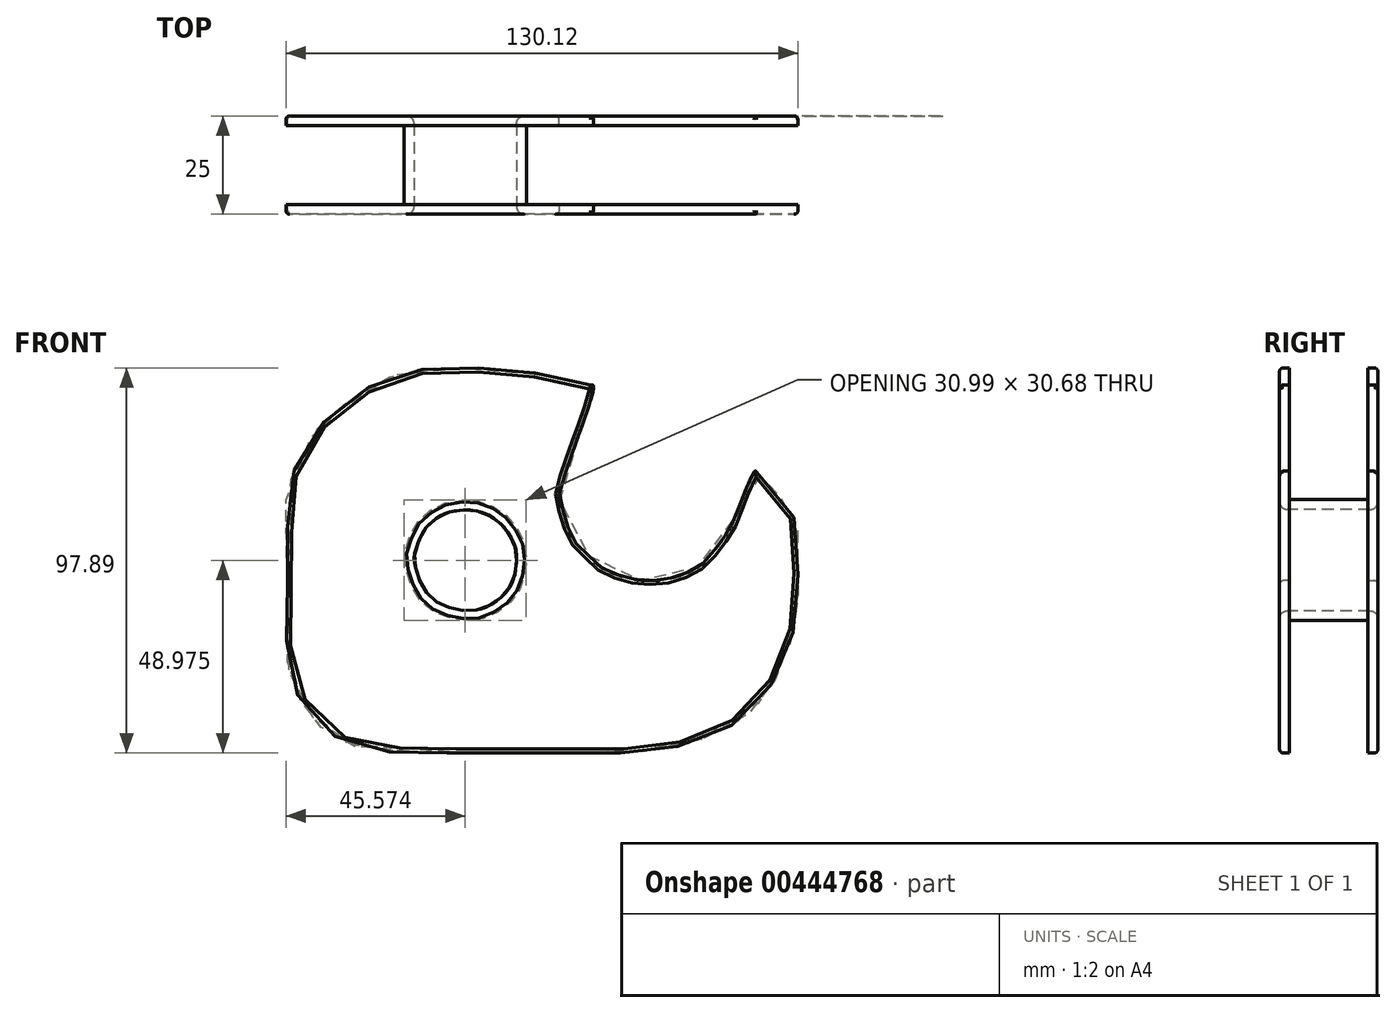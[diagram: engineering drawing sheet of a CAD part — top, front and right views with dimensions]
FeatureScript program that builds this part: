
annotation { "Feature Type Name" : "Feature", "Feature Type Description" : "" }
export const myFeature = defineFeature(function(context is Context, id is Id, definition is map)
    precondition{}
    {
        {
            var Q0;
            Q0=qCreatedBy(makeId("Front.planeOp"),FACE);
            var sketch = newSketch(context, id + "F0", { "sketchPlane" : qUnion([Q0])});
            skFitSpline(sketch, "E0", {"points": [v(-71.65, 26.42) * mm, v(-80.15, 0) * mm, v(-79.73, -4.2) * mm, v(-76.75, -12.5) * mm, v(-73.35, -16.11) * mm, v(-70.34, -19.08) * mm, v(-65.01, -21.68) * mm, v(-59.83, -22.83) * mm, v(-54.07, -22.76) * mm, v(-49.03, -21.39) * mm, v(-44.13, -18.8) * mm, v(-40.46, -14.7) * mm, v(-37.3, -10.23) * mm, v(-33.91, -2.3) * mm, v(-30.52, 4.9) * mm, v(-30.23, 4.68) * mm, v(-29.6, 4.1) * mm, v(-28.61, 3.17) * mm, v(-25.13, -0.54) * mm, v(-21.54, -5.47) * mm, v(-20.03, -8.48) * mm, v(-19.8, -11.5) * mm, v(-19.69, -25.69) * mm, v(-19.98, -30.15) * mm, v(-20.5, -33.92) * mm, v(-21.2, -37.17) * mm, v(-24.25, -46.03) * mm, v(-27.58, -50.92) * mm, v(-30.7, -55.25) * mm, v(-35.14, -58.91) * mm, v(-42.69, -62.76) * mm, v(-51.54, -65.35) * mm, v(-59.4, -66.43) * mm, v(-67.19, -66.7) * mm, v(-123.65, -66.4) * mm, v(-130.85, -65.55) * mm, v(-134.45, -64.1) * mm, v(-138.48, -61.87) * mm, v(-141.22, -59.78) * mm, v(-143.02, -57.55) * mm, v(-144.53, -55.54) * mm, v(-147.41, -50.86) * mm, v(-148.85, -46.68) * mm, v(-149.43, -43.08) * mm, v(-149.64, -40.27) * mm, v(-149.44, -8.11) * mm, v(-149.44, 0) * mm, v(-143.27, 13.63) * mm, v(-139.85, 17.57) * mm, v(-134.7, 22.02) * mm, v(-127.52, 26.82) * mm, v(-121.35, 29.56) * mm, v(-114.84, 30.76) * mm, v(-110.6, 31.06) * mm, v(-97.42, 30.92) * mm, v(-86.18, 29.77) * mm, v(-80.71, 28.62) * mm, v(-77.4, 27.9) * mm, v(-72.93, 26.74) * mm, v(-71.65, 26.42) * mm]});
            skSolve(sketch);
        }
        {
            var Q0;
            Q0=makeQuery(id+"F0.imprint","IMPRINT",FACE,{"disambiguationData":[TD([[makeQuery(id+"F0.imprint","IMPRINT",EDGE,{"derivedFrom":sQuery(id+"F0.wireOp",EDGE,"E0")}),-1.0]])]});
            var sketch = newSketch(context, id + "F1", { "sketchPlane" : qUnion([Q0])});
            skFitSpline(sketch, "E1", {"points": [v(-104.6, -4.98) * mm, v(-104.12, -4.9) * mm, v(-102.76, -5.01) * mm, v(-101.52, -5.2) * mm, v(-100.25, -5.56) * mm, v(-99.03, -5.95) * mm, v(-96.86, -7.2) * mm, v(-94.55, -9.13) * mm, v(-92.59, -12) * mm, v(-91.25, -15.64) * mm, v(-91.34, -19.3) * mm, v(-91.7, -21.7) * mm, v(-92.68, -24.2) * mm, v(-94.73, -26.9) * mm, v(-99.43, -29.92) * mm, v(-103.55, -30.64) * mm, v(-107.66, -30) * mm, v(-112.4, -27.77) * mm, v(-115, -24.56) * mm, v(-116.06, -22.14) * mm, v(-117.14, -18.03) * mm, v(-117.14, -16.42) * mm, v(-116.78, -15.26) * mm, v(-116.42, -14) * mm, v(-115.63, -11.94) * mm, v(-114.55, -9.93) * mm, v(-112.13, -7.6) * mm, v(-109.14, -5.78) * mm, v(-106.1, -5.17) * mm, v(-104.6, -4.98) * mm]});
            skSolve(sketch);
        }
        {
            var Q0;
            Q0=makeQuery(id+"F1.imprint","IMPRINT",FACE,{"disambiguationData":[TD([[makeQuery(id+"F1.imprint","IMPRINT",EDGE,{"derivedFrom":sQuery(id+"F1.wireOp",EDGE,"E1")}),1.0]])]});
            extrude(context, id + "F2", {"entities" : qUnion([Q0]), "depth" : 25 * mm});
        }
        {
            var Q0;
            Q0=makeQuery(id+"F2.opExtrude","SWEPT_FACE",FACE,{"disambiguationData":[OSD([sQuery(id+"F0.wireOp",EDGE,"E0")])]});
            shell(context, id + "F3", {"entities" : qUnion([Q0]), "thickness" : 2.5 * mm});
        }
        {
            var Q0;
            Q0=makeQuery(id+"F2.opExtrude","CAP_EDGE",EDGE,{"disambiguationData":[OSD([sQuery(id+"F1.wireOp",EDGE,"E1")])],"isStart":false});
            var Q1;
            Q1=makeQuery(id+"F2.opExtrude","CAP_EDGE",EDGE,{"disambiguationData":[OSD([sQuery(id+"F1.wireOp",EDGE,"E1")])],"isStart":true});
            fillet(context, id + "F4", {"entities" : qUnion([Q0, Q1]), "radius" : 2 * mm, "tangentPropagation" : true, "allowEdgeOverflow" : false});
        }
        {
            var Q0;
            Q0=makeQuery(id+"F2.opExtrude","CAP_EDGE",EDGE,{"disambiguationData":[OSD([sQuery(id+"F0.wireOp",EDGE,"E0")])],"isStart":false});
            var Q1;
            Q1=makeQuery(id+"F2.opExtrude","CAP_EDGE",EDGE,{"disambiguationData":[OSD([sQuery(id+"F0.wireOp",EDGE,"E0")])],"isStart":true});
            fillet(context, id + "F5", {"entities" : qUnion([Q0, Q1]), "radius" : 1 * mm, "tangentPropagation" : true, "allowEdgeOverflow" : false});
        }
    });
